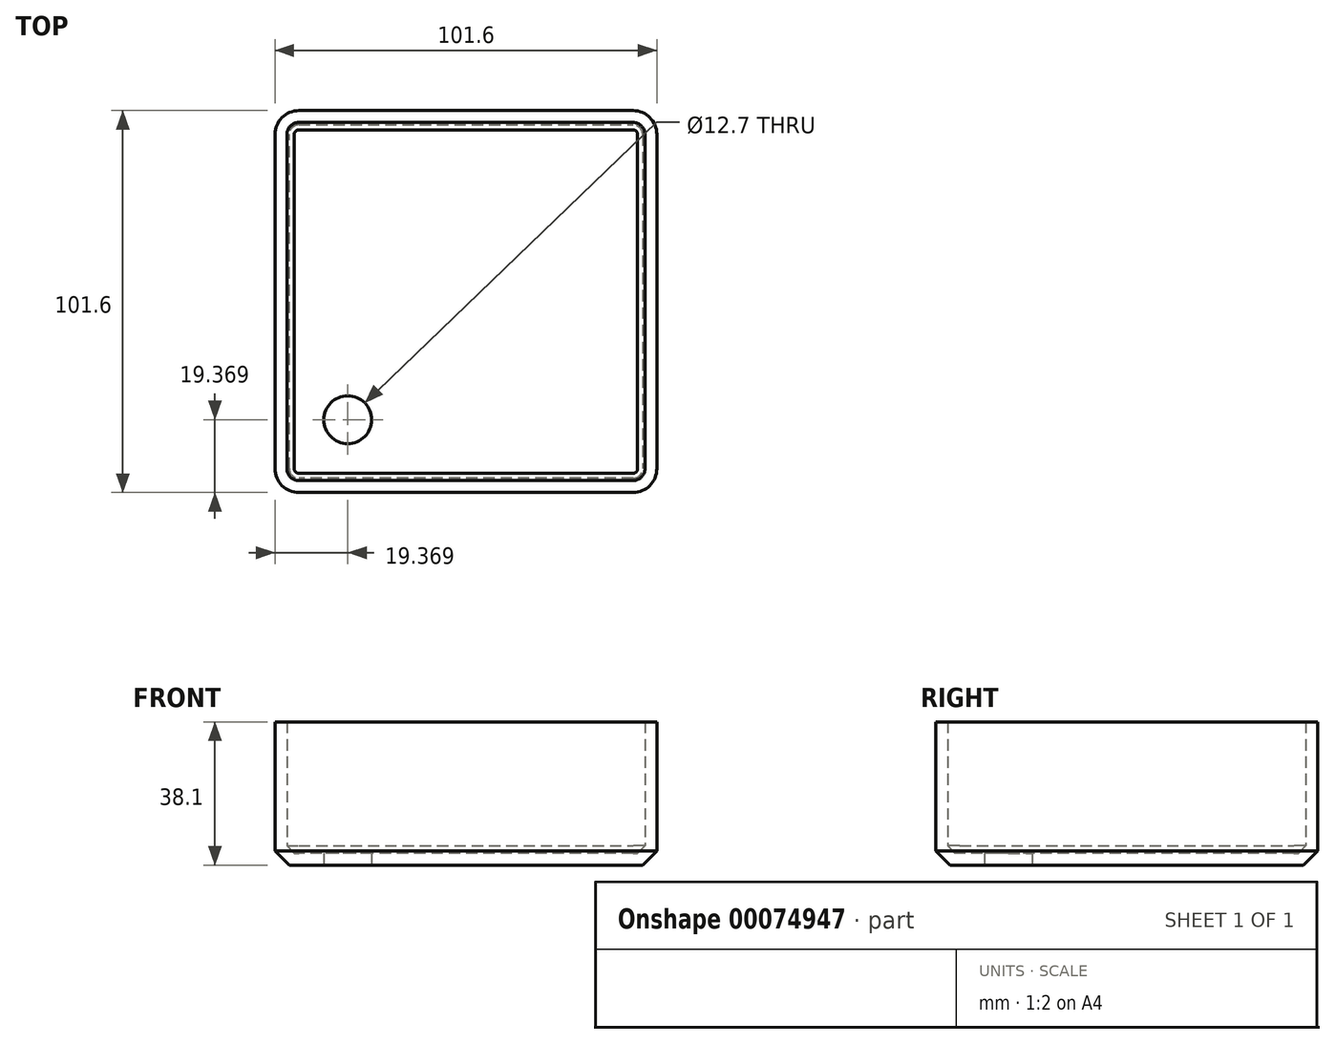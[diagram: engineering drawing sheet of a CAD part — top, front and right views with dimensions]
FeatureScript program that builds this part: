
annotation { "Feature Type Name" : "Feature", "Feature Type Description" : "" }
export const myFeature = defineFeature(function(context is Context, id is Id, definition is map)
    precondition{}
    {
        {
            var Q0;
            Q0=qCreatedBy(makeId("Top.planeOp"),FACE);
            var sketch = newSketch(context, id + "F0", { "sketchPlane" : qUnion([Q0])});
            skLineSegment(sketch, "E0.rect.bottom", {"start": v(50.8, 50.8) * mm, "end": v(-50.8, 50.8) * mm});
            skLineSegment(sketch, "E0.rect.top", {"start": v(50.8, -50.8) * mm, "end": v(-50.8, -50.8) * mm});
            skLineSegment(sketch, "E0.rect.left", {"start": v(50.8, 50.8) * mm, "end": v(50.8, -50.8) * mm});
            skLineSegment(sketch, "E0.rect.right", {"start": v(-50.8, 50.8) * mm, "end": v(-50.8, -50.8) * mm});
            skPoint(sketch, "E0.rect.middle", {"position": v(0, 0) * mm});
            skSolve(sketch);
        }
        {
            var Q0;
            Q0 = qSketchRegion(id + "F0", true);
            extrude(context, id + "F1", {"entities" : qUnion([Q0]), "depth" : 38.1 * mm});
        }
        {
            var Q0;
            Q0=makeQuery(id+"F1.opExtrude","CAP_FACE",FACE,{"disambiguationData":[OSD([sQuery(id+"F0.wireOp",EDGE,"E0.rect.bottom"),sQuery(id+"F0.wireOp",EDGE,"E0.rect.top"),sQuery(id+"F0.wireOp",EDGE,"E0.rect.left"),sQuery(id+"F0.wireOp",EDGE,"E0.rect.right")])],"isStart":true});
            var sketch = newSketch(context, id + "F2", { "sketchPlane" : qUnion([Q0])});
            skCircle(sketch, "E1", {"center": v(-31.43, 31.43) * mm, "radius": 6.35 * mm});
            skLineSegment(sketch, "E2", {"start": v(-31.43, 31.43) * mm, "end": v(0, 0) * mm, "construction": true});
            skSolve(sketch);
        }
        {
            var Q0;
            Q0=makeQuery(id+"F1.opExtrude","SWEPT_EDGE",EDGE,{"disambiguationData":[OSD([sQuery(id+"F0.wireOp",EDGE,"E0.rect.top"),sQuery(id+"F0.wireOp",EDGE,"E0.rect.left")])]});
            var Q1;
            Q1=makeQuery(id+"F1.opExtrude","SWEPT_EDGE",EDGE,{"disambiguationData":[OSD([sQuery(id+"F0.wireOp",EDGE,"E0.rect.bottom"),sQuery(id+"F0.wireOp",EDGE,"E0.rect.left")])]});
            var Q2;
            Q2=makeQuery(id+"F1.opExtrude","SWEPT_EDGE",EDGE,{"disambiguationData":[OSD([sQuery(id+"F0.wireOp",EDGE,"E0.rect.bottom"),sQuery(id+"F0.wireOp",EDGE,"E0.rect.right")])]});
            var Q3;
            Q3=makeQuery(id+"F1.opExtrude","SWEPT_EDGE",EDGE,{"disambiguationData":[OSD([sQuery(id+"F0.wireOp",EDGE,"E0.rect.top"),sQuery(id+"F0.wireOp",EDGE,"E0.rect.right")])]});
            fillet(context, id + "F3", {"entities" : qUnion([Q0, Q1, Q2, Q3]), "radius" : 6.35 * mm, "tangentPropagation" : true, "allowEdgeOverflow" : false});
        }
        {
            var Q0;
            Q0=makeQuery(id+"F1.opExtrude","CAP_EDGE",EDGE,{"disambiguationData":[OSD([sQuery(id+"F0.wireOp",EDGE,"E0.rect.left")])],"isStart":true});
            chamfer(context, id + "F4", {"entities" : qUnion([Q0]), "width" : 3.8 * mm, "tangentPropagation" : true});
        }
        {
            var Q0;
            Q0=makeQuery(id+"F1.opExtrude","CAP_FACE",FACE,{"disambiguationData":[OSD([sQuery(id+"F0.wireOp",EDGE,"E0.rect.bottom"),sQuery(id+"F0.wireOp",EDGE,"E0.rect.top"),sQuery(id+"F0.wireOp",EDGE,"E0.rect.left"),sQuery(id+"F0.wireOp",EDGE,"E0.rect.right")])],"isStart":false});
            shell(context, id + "F5", {"entities" : qUnion([Q0]), "thickness" : 3.17 * mm});
        }
        {
            var Q0;
            Q0 = qSketchRegion(id + "F2", true);
            extrude(context, id + "F6", {"entities" : qUnion([Q0]), "operationType" : NewBodyOperationType.REMOVE, "endBound" : BoundingType.THROUGH_ALL, "oppositeDirection" : true, "depth" : 2.54 * mm});
        }
    });
